# Revit family: 1Electronics_Amplifier_Biamp_Commercial-Audio-Mixing-Amplifiers_MA65
name_source: partatom
category: Communication Devices
units: mm (PartAtom-declared; Revit-internal decimal feet)

## family parameters
Cut with Voids When Loaded = No
Host = Face
Maintain Annotation Orientation = No
OmniClass Number = 23.85.10.11.14
OmniClass Title = Audio Equipment
Part Type = Normal
Room Calculation Point = No
Round Connector Dimension = Use Diameter
Shared = No

## types (1)
- MA65
    Apparent Load = 170 VA
    Applicable low impedance = Yes
    Chime = Yes
    Connector Description = 24V DC(Euroblock) - 230V AC
    Cooling system = Convection
    Default Elevation = 4' - 0"
    Depth = 1' - 7"
    Description = MA65 Compact Mixing Amplifier, 65W @ 100 Volt
    Emergency power supply = 24 VDC
    Frequency response (in Hz) = 60 - 18 k
    Height = 0' - 3 1/2"
    Housing Material = Biamp - Metal - Black
    Inputs with Phantom power = 3
    Line input unbalanced = 2
    MIC inputs balanced = 3
    Manufacturer = Biamp
    Max Power Consumption = 170 W
    Minimum impedance load in ohms = 8
    Model = MA65
    Number of Poles = 1
    Output power tappings = 100 - 70 volts - 8 ohms
    Power Factor = 1
    Priority levels = 2
    Priority switch = 1
    Product Documentation Link = https://downloads.biamp.com
    Product Page URL = https://www.biamp.com
    Product data url = https://www.bimobject.com
    Tone control = Yes
    URL = https://www.biamp.com
    VOX mute = Yes
    Voltage = 120 V
    Weight = 13.01 lb
    Width = 0' - 10 1/2"
    Zone outputs = 1

## geometry (parser evidence)
native form markers: Sweep x9
no freeform markers — native parametric forms only
